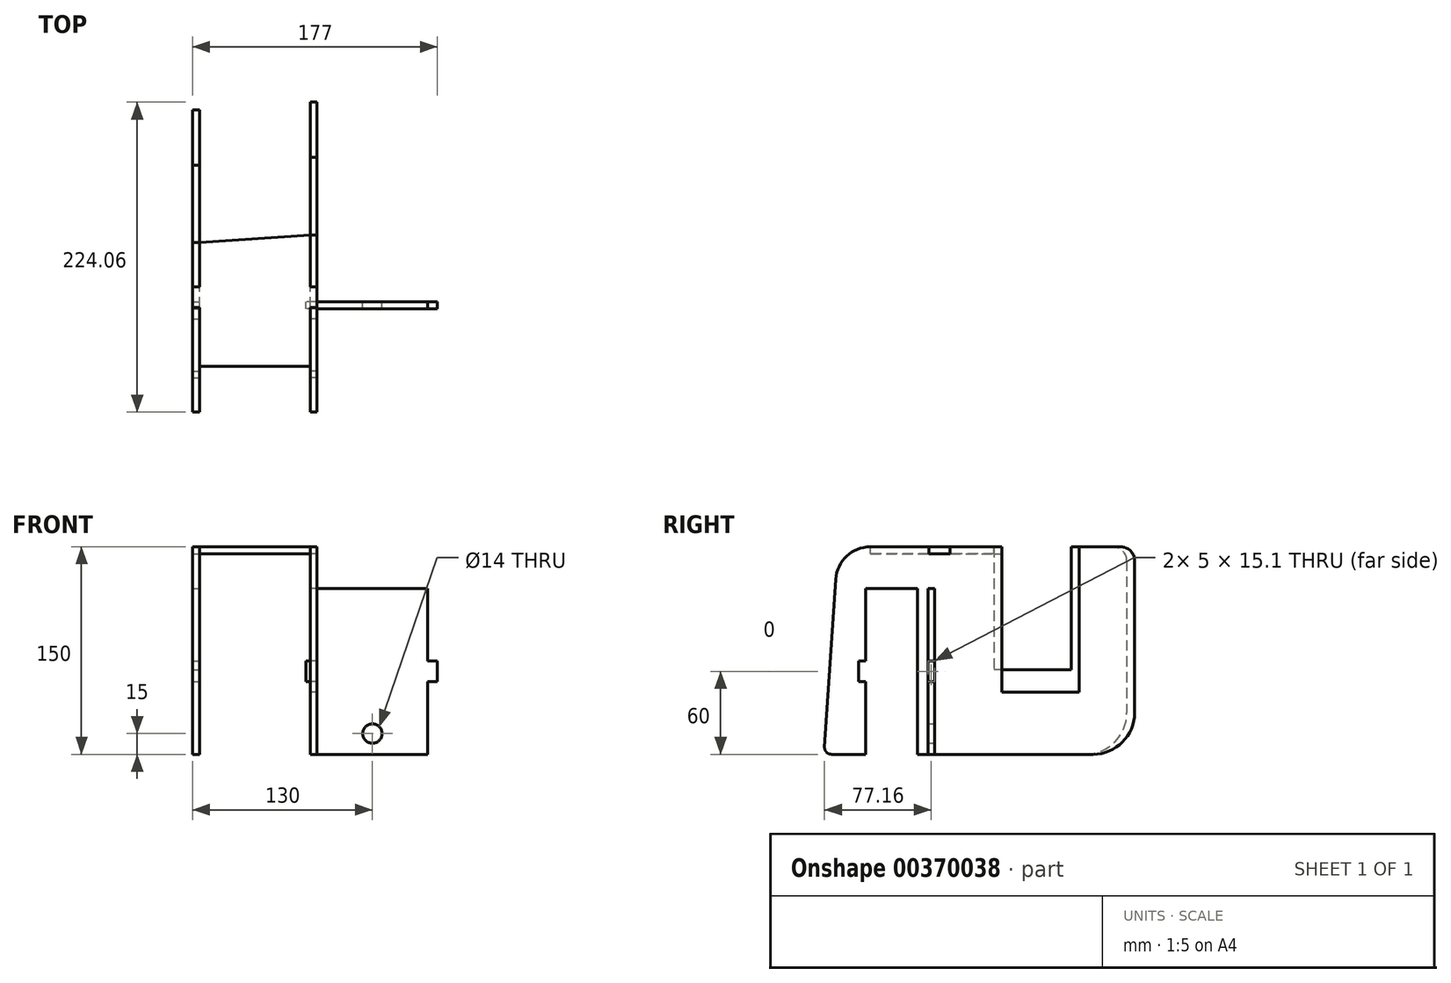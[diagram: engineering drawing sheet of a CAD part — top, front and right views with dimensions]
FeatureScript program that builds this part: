
annotation { "Feature Type Name" : "Feature", "Feature Type Description" : "" }
export const myFeature = defineFeature(function(context is Context, id is Id, definition is map)
    precondition{}
    {
        {
            var Q0;
            Q0=qCreatedBy(makeId("Right.planeOp"),FACE);
            var sketch = newSketch(context, id + "F0", { "sketchPlane" : qUnion([Q0])});
            skLineSegment(sketch, "E0.bottom", {"start": v(0, 0) * mm, "end": v(66, 0) * mm, "construction": true});
            skLineSegment(sketch, "E0.top", {"start": v(0, -105) * mm, "end": v(66, -105) * mm, "construction": true});
            skLineSegment(sketch, "E0.left", {"start": v(0, 0) * mm, "end": v(0, -105) * mm, "construction": true});
            skLineSegment(sketch, "E0.right", {"start": v(66, 0) * mm, "end": v(66, -105) * mm, "construction": true});
            skLineSegment(sketch, "E1", {"start": v(5, 0) * mm, "end": v(5, -105) * mm});
            skLineSegment(sketch, "E2", {"start": v(5, -105) * mm, "end": v(61, -105) * mm});
            skLineSegment(sketch, "E3", {"start": v(61, -105) * mm, "end": v(61, 0) * mm});
            skLineSegment(sketch, "E4", {"start": v(61, 0) * mm, "end": v(91, 0) * mm});
            skLineSegment(sketch, "E5", {"start": v(101, -10) * mm, "end": v(101, -120) * mm});
            skLineSegment(sketch, "E6", {"start": v(71, -150) * mm, "end": v(-48.4, -150) * mm});
            skLineSegment(sketch, "E7", {"start": v(-48.4, -150) * mm, "end": v(-48.4, -97.55) * mm, "construction": true});
            skLineSegment(sketch, "E8", {"start": v(-48.4, -30) * mm, "end": v(-93.4, -30) * mm});
            skLineSegment(sketch, "E9", {"start": v(-93.4, -30) * mm, "end": v(-93.4, -82.45) * mm});
            skLineSegment(sketch, "E10", {"start": v(-93.4, -150) * mm, "end": v(-118.06, -150) * mm});
            skLineSegment(sketch, "E11", {"start": v(-123.04, -144.67) * mm, "end": v(-114.96, -23.34) * mm});
            skLineSegment(sketch, "E12", {"start": v(-90.01, 0) * mm, "end": v(0, 0) * mm});
            skLineSegment(sketch, "E13.bottom", {"start": v(-93.4, -82.45) * mm, "end": v(-98.4, -82.45) * mm});
            skLineSegment(sketch, "E13.top", {"start": v(-93.4, -97.55) * mm, "end": v(-98.4, -97.55) * mm});
            skLineSegment(sketch, "E13.right", {"start": v(-98.4, -82.45) * mm, "end": v(-98.4, -97.55) * mm});
            skLineSegment(sketch, "E14.bottom", {"start": v(-48.4, -82.45) * mm, "end": v(-43.4, -82.45) * mm});
            skLineSegment(sketch, "E14.top", {"start": v(-48.4, -97.55) * mm, "end": v(-43.4, -97.55) * mm});
            skLineSegment(sketch, "E14.right", {"start": v(-43.4, -82.45) * mm, "end": v(-43.4, -97.55) * mm});
            skPoint(sketch, "E15", {"position": v(-93.4, -90) * mm});
            skPoint(sketch, "E16", {"position": v(-48.4, -90) * mm});
            skLineSegment(sketch, "E17.trimOffspring", {"start": v(-93.4, -97.55) * mm, "end": v(-93.4, -150) * mm});
            skLineSegment(sketch, "E18.trimOffspring", {"start": v(-48.4, -82.45) * mm, "end": v(-48.4, -30) * mm, "construction": true});
            skLineSegment(sketch, "E19", {"start": v(-90.01, 0) * mm, "end": v(5, 0) * mm});
            skPoint(sketch, "E20.visualSharp", {"position": v(101, -150) * mm});
            skArc(sketch, "E20.filletArc", {"start": v(71, -150) * mm, "mid": v(92.21, -141.21) * mm, "end": v(101, -120) * mm});
            skPoint(sketch, "E21.visualSharp", {"position": v(101, 0) * mm});
            skArc(sketch, "E21.filletArc", {"start": v(101, -10) * mm, "mid": v(98.07, -2.93) * mm, "end": v(91, 0) * mm});
            skPoint(sketch, "E22.visualSharp", {"position": v(-113.4, 0) * mm});
            skArc(sketch, "E22.filletArc", {"start": v(-90.01, 0) * mm, "mid": v(-107.1, -6.74) * mm, "end": v(-114.96, -23.34) * mm});
            skPoint(sketch, "E23.visualSharp", {"position": v(-123.4, -150) * mm});
            skArc(sketch, "E23.filletArc", {"start": v(-123.04, -144.67) * mm, "mid": v(-121.7, -148.42) * mm, "end": v(-118.06, -150) * mm});
            skPoint(sketch, "E24", {"position": v(-70.9, -30) * mm});
            skPoint(sketch, "E25", {"position": v(-169.24, -72.15) * mm});
            skLineSegment(sketch, "E26", {"start": v(-60.9, -30) * mm, "end": v(-60.9, -150) * mm, "construction": true});
            skLineSegment(sketch, "E27", {"start": v(-55.9, -30) * mm, "end": v(-55.9, -150) * mm});
            skLineSegment(sketch, "E28", {"start": v(-55.9, -150) * mm, "end": v(-48.4, -150) * mm});
            skLineSegment(sketch, "E29", {"start": v(-48.4, -82.45) * mm, "end": v(-48.4, -97.55) * mm});
            skPoint(sketch, "E30", {"position": v(-47.51, 0) * mm});
            skLineSegment(sketch, "E31", {"start": v(-47.51, 0) * mm, "end": v(-47.51, -5) * mm});
            skLineSegment(sketch, "E32", {"start": v(-47.51, -5) * mm, "end": v(-32.41, -5) * mm});
            skLineSegment(sketch, "E33", {"start": v(-32.41, -5) * mm, "end": v(-32.41, 0) * mm});
            skSolve(sketch);
        }
        {
            var Q0;
            {var subQ2=sQuery(id+"F0.wireOp",EDGE,"E1");Q0=makeQuery(id+"F0.imprint","IMPRINT",FACE,{"disambiguationData":[TD([[makeQuery(id+"F0.imprint","IMPRINT",EDGE,{"derivedFrom":subQ2}),-1.0]])]});}
            extrude(context, id + "F1", {"entities" : qUnion([Q0]), "depth" : 5 * mm});
        }
        {
            var Q0;
            Q0=makeQuery(id+"F1.opExtrude","SWEPT_FACE",FACE,{"disambiguationData":[OSD([sQuery(id+"F0.wireOp",EDGE,"E14.right")])]});
            var sketch = newSketch(context, id + "F2", { "sketchPlane" : qUnion([Q0])});
            skLineSegment(sketch, "E34.bottom", {"start": v(5, -30) * mm, "end": v(85, -30) * mm});
            skLineSegment(sketch, "E34.top", {"start": v(5, -150) * mm, "end": v(85, -150) * mm});
            skLineSegment(sketch, "E34.left", {"start": v(5, -30) * mm, "end": v(5, -150) * mm});
            skLineSegment(sketch, "E34.right", {"start": v(85, -30) * mm, "end": v(85, -150) * mm});
            skLineSegment(sketch, "E35.bottom", {"start": v(5, -82.5) * mm, "end": v(-3, -82.5) * mm});
            skLineSegment(sketch, "E35.top", {"start": v(5, -97.5) * mm, "end": v(-3, -97.5) * mm});
            skLineSegment(sketch, "E35.left", {"start": v(5, -82.5) * mm, "end": v(5, -97.5) * mm});
            skLineSegment(sketch, "E35.right", {"start": v(-3, -82.5) * mm, "end": v(-3, -97.5) * mm});
            skLineSegment(sketch, "E36.bottom", {"start": v(85, -82.5) * mm, "end": v(92, -82.5) * mm});
            skLineSegment(sketch, "E36.top", {"start": v(85, -97.5) * mm, "end": v(92, -97.5) * mm});
            skLineSegment(sketch, "E36.left", {"start": v(85, -82.5) * mm, "end": v(85, -97.5) * mm});
            skLineSegment(sketch, "E36.right", {"start": v(92, -82.5) * mm, "end": v(92, -97.5) * mm});
            skCircle(sketch, "E37", {"center": v(45, -135) * mm, "radius": 7 * mm});
            skPoint(sketch, "E38", {"position": v(45, -30) * mm});
            skPoint(sketch, "E39", {"position": v(85, -90) * mm});
            skSolve(sketch);
        }
        {
            var Q0;
            Q0=qSketchRegion(id+"F2",true);
            extrude(context, id + "F3", {"entities" : qUnion([Q0]), "depth" : 5 * mm});
        }
        {
            var Q0;
            Q0=qCreatedBy(makeId("Right.planeOp"),FACE);
            cPlane(context, id + "F4", {"entities" : qUnion([Q0]), "cplaneType" : CPlaneType.OFFSET, "offset" : 80 * mm, "oppositeDirection" : true, "width" : 150 * mm, "height" : 150 * mm});
        }
        {
            var Q0;
            Q0=qCreatedBy(id+"F4.planeOp",FACE);
            var sketch = newSketch(context, id + "F5", { "sketchPlane" : qUnion([Q0])});
            skLineSegment(sketch, "E40.bottom", {"start": v(-5.6, 0) * mm, "end": v(60.4, 0) * mm, "construction": true});
            skLineSegment(sketch, "E40.top", {"start": v(-5.6, -105) * mm, "end": v(60.4, -105) * mm, "construction": true});
            skLineSegment(sketch, "E40.left", {"start": v(-5.6, 0) * mm, "end": v(-5.6, -105) * mm, "construction": true});
            skLineSegment(sketch, "E40.right", {"start": v(60.4, 0) * mm, "end": v(60.4, -105) * mm, "construction": true});
            skLineSegment(sketch, "E41", {"start": v(-0.6, 0) * mm, "end": v(-0.6, -105) * mm});
            skLineSegment(sketch, "E42", {"start": v(-0.6, -105) * mm, "end": v(55.4, -105) * mm});
            skLineSegment(sketch, "E43", {"start": v(55.4, -105) * mm, "end": v(55.4, 0) * mm});
            skLineSegment(sketch, "E44", {"start": v(55.4, 0) * mm, "end": v(85.4, 0) * mm});
            skLineSegment(sketch, "E45", {"start": v(95.4, -10) * mm, "end": v(95.4, -120) * mm});
            skLineSegment(sketch, "E46", {"start": v(65.4, -150) * mm, "end": v(-48.4, -150) * mm});
            skLineSegment(sketch, "E47", {"start": v(-48.4, -150) * mm, "end": v(-48.4, -97.55) * mm, "construction": true});
            skLineSegment(sketch, "E48", {"start": v(-48.4, -30) * mm, "end": v(-93.4, -30) * mm});
            skLineSegment(sketch, "E49", {"start": v(-93.4, -30) * mm, "end": v(-93.4, -82.45) * mm});
            skLineSegment(sketch, "E50", {"start": v(-93.4, -150) * mm, "end": v(-118.06, -150) * mm});
            skLineSegment(sketch, "E51", {"start": v(-123.04, -144.67) * mm, "end": v(-114.96, -23.34) * mm});
            skLineSegment(sketch, "E52", {"start": v(-90.01, 0) * mm, "end": v(-5.6, 0) * mm});
            skLineSegment(sketch, "E53.bottom", {"start": v(-93.4, -82.45) * mm, "end": v(-98.4, -82.45) * mm});
            skLineSegment(sketch, "E53.top", {"start": v(-93.4, -97.55) * mm, "end": v(-98.4, -97.55) * mm});
            skLineSegment(sketch, "E53.right", {"start": v(-98.4, -82.45) * mm, "end": v(-98.4, -97.55) * mm});
            skLineSegment(sketch, "E54.bottom", {"start": v(-48.4, -82.45) * mm, "end": v(-43.4, -82.45) * mm});
            skLineSegment(sketch, "E54.top", {"start": v(-48.4, -97.55) * mm, "end": v(-43.4, -97.55) * mm});
            skLineSegment(sketch, "E54.right", {"start": v(-43.4, -82.45) * mm, "end": v(-43.4, -97.55) * mm});
            skPoint(sketch, "E55", {"position": v(-93.4, -90) * mm});
            skPoint(sketch, "E56", {"position": v(-48.4, -90) * mm});
            skLineSegment(sketch, "E57.trimOffspring", {"start": v(-93.4, -97.55) * mm, "end": v(-93.4, -150) * mm});
            skLineSegment(sketch, "E58.trimOffspring", {"start": v(-48.4, -82.45) * mm, "end": v(-48.4, -30) * mm, "construction": true});
            skLineSegment(sketch, "E59", {"start": v(-90.01, 0) * mm, "end": v(-0.6, 0) * mm});
            skPoint(sketch, "E60.visualSharp", {"position": v(95.4, -150) * mm});
            skArc(sketch, "E60.filletArc", {"start": v(65.4, -150) * mm, "mid": v(86.61, -141.21) * mm, "end": v(95.4, -120) * mm});
            skPoint(sketch, "E61.visualSharp", {"position": v(95.4, 0) * mm});
            skArc(sketch, "E61.filletArc", {"start": v(95.4, -10) * mm, "mid": v(92.47, -2.93) * mm, "end": v(85.4, 0) * mm});
            skPoint(sketch, "E62.visualSharp", {"position": v(-113.4, 0) * mm});
            skArc(sketch, "E62.filletArc", {"start": v(-90.01, 0) * mm, "mid": v(-107.1, -6.74) * mm, "end": v(-114.96, -23.34) * mm});
            skPoint(sketch, "E63.visualSharp", {"position": v(-123.4, -150) * mm});
            skArc(sketch, "E63.filletArc", {"start": v(-123.04, -144.67) * mm, "mid": v(-121.7, -148.42) * mm, "end": v(-118.06, -150) * mm});
            skPoint(sketch, "E64", {"position": v(-70.9, -30) * mm});
            skPoint(sketch, "E65", {"position": v(-146.28, 4.13) * mm});
            skLineSegment(sketch, "E66", {"start": v(-60.9, -30) * mm, "end": v(-60.9, -150) * mm, "construction": true});
            skLineSegment(sketch, "E67", {"start": v(-55.9, -30) * mm, "end": v(-55.9, -150) * mm});
            skLineSegment(sketch, "E68", {"start": v(-55.9, -150) * mm, "end": v(-48.4, -150) * mm});
            skLineSegment(sketch, "E69", {"start": v(-48.4, -82.45) * mm, "end": v(-48.4, -97.55) * mm});
            skPoint(sketch, "E70", {"position": v(55.4, -89) * mm});
            skLineSegment(sketch, "E71", {"start": v(55.4, -89) * mm, "end": v(-0.6, -89) * mm});
            skPoint(sketch, "E72", {"position": v(-47.51, 0) * mm});
            skLineSegment(sketch, "E73", {"start": v(-47.51, 0) * mm, "end": v(-47.51, -5) * mm});
            skLineSegment(sketch, "E74", {"start": v(-47.51, -5) * mm, "end": v(-32.41, -5) * mm});
            skLineSegment(sketch, "E75", {"start": v(-32.41, -5) * mm, "end": v(-32.41, 0) * mm});
            skSolve(sketch);
        }
        {
            var Q0;
            {var subQ0=sQuery(id+"F5.wireOp",EDGE,"E42");Q0=makeQuery(id+"F5.imprint","IMPRINT",FACE,{"disambiguationData":[TD([[makeQuery(id+"F5.imprint","IMPRINT",EDGE,{"derivedFrom":subQ0}),1.0]])]});}
            var Q1;
            {var subQ7=sQuery(id+"F5.wireOp",EDGE,"E42");Q1=makeQuery(id+"F5.imprint","IMPRINT",FACE,{"disambiguationData":[TD([[makeQuery(id+"F5.imprint","IMPRINT",EDGE,{"derivedFrom":subQ7}),-1.0]])]});}
            extrude(context, id + "F6", {"entities" : qUnion([Q0, Q1]), "oppositeDirection" : true, "depth" : 5 * mm});
        }
        {
            var Q0;
            Q0=qCreatedBy(makeId("Top.planeOp"),FACE);
            var sketch = newSketch(context, id + "F7", { "sketchPlane" : qUnion([Q0])});
            skLineSegment(sketch, "E76.0", {"start": v(-85, -90.01) * mm, "end": v(-80, -90.01) * mm, "construction": true});
            skLineSegment(sketch, "E77.0", {"start": v(5, -90.01) * mm, "end": v(0, -90.01) * mm, "construction": true});
            skLineSegment(sketch, "E78.0", {"start": v(5, 5) * mm, "end": v(0, 5) * mm, "construction": true});
            skLineSegment(sketch, "E79.0", {"start": v(-85, -0.6) * mm, "end": v(-80, -0.6) * mm, "construction": true});
            skLineSegment(sketch, "E80", {"start": v(0, -90.01) * mm, "end": v(0, 5) * mm});
            skLineSegment(sketch, "E81", {"start": v(-80, -0.6) * mm, "end": v(0, 5) * mm});
            skLineSegment(sketch, "E82", {"start": v(-80, -0.6) * mm, "end": v(-80, -90.01) * mm});
            skLineSegment(sketch, "E83", {"start": v(-80, -90.01) * mm, "end": v(0, -90.01) * mm});
            skPoint(sketch, "E84", {"position": v(0, -47.49) * mm});
            skLineSegment(sketch, "E85", {"start": v(0, -47.49) * mm, "end": v(5, -47.49) * mm});
            skLineSegment(sketch, "E86", {"start": v(5, -47.49) * mm, "end": v(5, -32.49) * mm});
            skLineSegment(sketch, "E87", {"start": v(5, -32.49) * mm, "end": v(0, -32.49) * mm});
            skLineSegment(sketch, "E88", {"start": v(-40, -90.01) * mm, "end": v(-40, 2.2) * mm, "construction": true});
            skLineSegment(sketch, "E89.MirrorCS", {"start": v(-85, -32.49) * mm, "end": v(-80, -32.49) * mm});
            skLineSegment(sketch, "E90.MirrorCS", {"start": v(-85, -47.49) * mm, "end": v(-85, -32.49) * mm});
            skLineSegment(sketch, "E91.MirrorCS", {"start": v(-80, -47.49) * mm, "end": v(-85, -47.49) * mm});
            skSolve(sketch);
        }
        {
            var Q0;
            Q0 = qSketchRegion(id + "F7", true);
            extrude(context, id + "F8", {"entities" : qUnion([Q0]), "oppositeDirection" : true, "depth" : 5 * mm});
        }
    });
